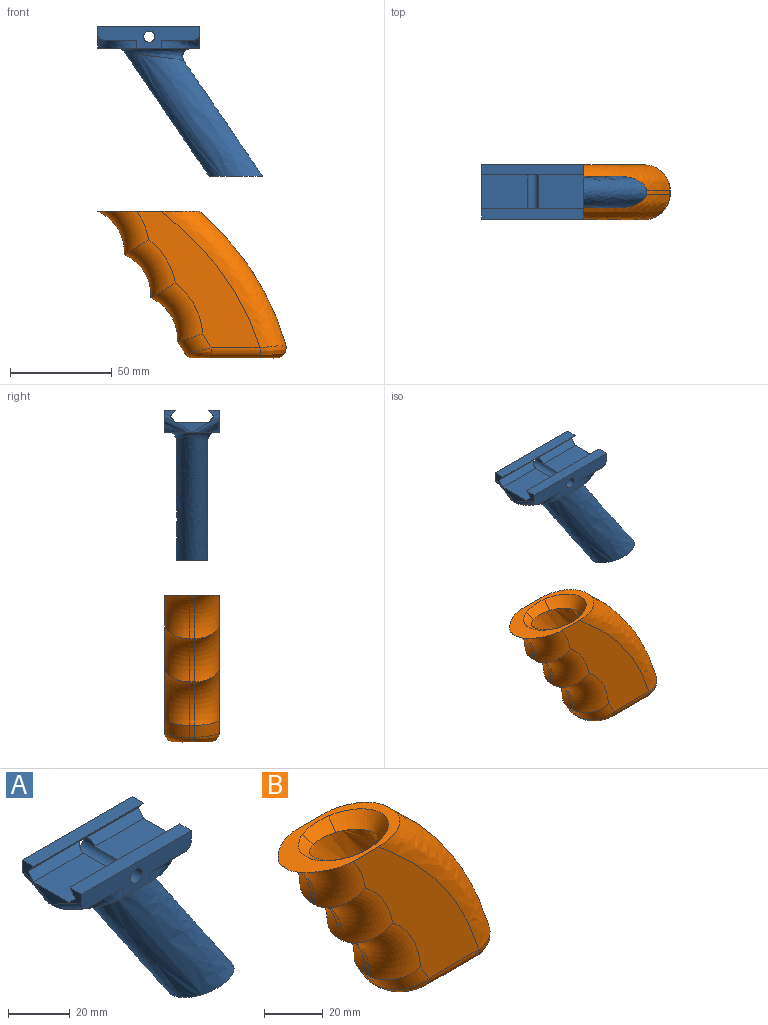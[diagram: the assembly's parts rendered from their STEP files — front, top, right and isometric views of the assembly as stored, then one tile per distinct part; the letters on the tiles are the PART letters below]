
ASSEMBLY  parts=2 mates=1
PART A: 27 faces, bbox 82.1x35.2x74.9 mm
  f0: plane 24x3.29mm, normal (0,0.77,0.64), area 89.2mm2, adj f1,f6,f9,f25
  f1: plane 22.68x16.5mm, normal (0,0,1), area 374.2mm2, adj f0,f6,f12,f25
  f2: plane 23.59x3.23mm, normal (0,-0.77,0.64), area 87.8mm2, adj f4,f11,f13,f25
  f3: plane 50.29x5.25mm, normal (0,0,1), area 264mm2, adj f4,f5,f6,f13
  f4: plane 27x11mm, normal (1,0,0), area 83.6mm2, adj f2,f3,f5,f7,f8,f9,f10,f11
  f5: plane 50.86x11.57mm, normal (0,1,0), area 373mm2, adj f3,f4,f6,f14,f17,f18,f21,f24
  f6: plane 27.33x11.33mm, normal (-1,0,0), area 78mm2, adj f0,f1,f3,f5,f7,f8,f9,f12
  f7: plane 50.86x11.57mm, normal (0,-1,0), area 372.8mm2, adj f4,f6,f8,f14,f15,f16,f22,f23
  f8: plane 50.29x5.25mm, normal (0,0,1), area 264mm2, adj f4,f6,f7,f9
  f9: plane 51.16x3.87mm, normal (0,0.77,-0.64), area 194.9mm2, adj f0,f4,f6,f8,f10,f25
  f10: plane 23.59x3.23mm, normal (0,0.77,0.64), area 87.8mm2, adj f4,f9,f11,f25
  f11: plane 22.33x16.5mm, normal (0,0,1), area 368.5mm2, adj f2,f4,f10,f25
  f12: plane 24x3.29mm, normal (0,-0.77,0.64), area 89.2mm2, adj f1,f6,f13,f25
  f13: plane 51.16x3.87mm, normal (0,-0.77,-0.64), area 194.9mm2, adj f2,f3,f4,f6,f12,f25
  f14: plane 50.72x27.43mm, normal (0,0,-1), area 466.7mm2, adj f4,f5,f6,f7,f15,f16,f17,f18
  f15: bspline ~22.9x10mm, area 89.5mm2, adj f7,f14,f23
  f16: bspline ~31.59x12.5mm, area 86.5mm2, adj f7,f14,f22
  f17: bspline ~31.59x12.5mm, area 89.7mm2, adj f5,f14,f21
  f18: bspline ~18.1x9.17mm, area 89.5mm2, adj f5,f14,f24
  f19: plane 26.94x15.99mm, normal (0,0,-1), area 318.5mm2, adj f20
  f20: bspline ~68.12x61.25mm, area 4200mm2, adj f19,f26
  f21: bspline ~14.67x7.7mm, area 40.7mm2, adj f4,f5,f14,f17
  f22: bspline ~16.64x8.51mm, area 40.8mm2, adj f4,f7,f14,f16
  f23: bspline ~17.09x9.64mm, area 45.5mm2, adj f6,f7,f14,f15
  f24: bspline ~16.58x9.36mm, area 45.5mm2, adj f5,f6,f14,f18
  f25: cylinder r=2.75mm len=27mm, axis (0,-1,0), area 263.8mm2, adj f0,f1,f2,f5,f7,f9,f10,f11
  f26: bspline ~36.01x23.37mm, area 493.5mm2, adj f14,f20
PART B: 33 faces, bbox 113.9x32.2x129.4 mm
  f0: plane 55.28x31.99mm, normal (0,0,1), area 457.1mm2, adj f1,f6,f7,f8,f9,f10,f14,f15
  f1: cylinder r=21.78mm len=21.32mm, axis (0,1,0), area 53.3mm2, adj f0,f2,f10,f15
  f2: cylinder r=21.78mm len=21.32mm, axis (0,1,0), area 53.3mm2, adj f1,f3,f11,f16
  f3: cylinder r=21.78mm len=21.32mm, axis (0,1,0), area 53.3mm2, adj f2,f4,f12,f17
  f4: plane 5.83x3.57mm, normal (-0.85,0,-0.52), area 13.7mm2, adj f3,f13,f18,f20
  f5: plane 40.69x17mm, normal (0,0,-1), area 638.3mm2, adj f19,f20,f21,f22,f23,f24,f25,f26
  f6: extruded ~65.77x42.23mm, area 158.5mm2, adj f0,f9,f14,f25
  f7: plane 67.22x60.73mm, normal (0,-1,0), area 1507.3mm2, adj f0,f14,f15,f16,f17,f18,f21
  f8: plane 67.22x60.73mm, normal (0,1,0), area 1507.2mm2, adj f0,f9,f10,f11,f12,f13,f24
  f9: bspline ~124.44x108.5mm, area 1621.5mm2, adj f0,f6,f8,f26
  f10: torus R=34.28mm, axis (0,-1,0), area 414.5mm2, adj f0,f1,f8,f11
  f11: torus R=34.28mm, axis (0,-1,0), area 498.7mm2, adj f2,f8,f10,f12
  f12: torus R=34.28mm, axis (0,-1,0), area 529.8mm2, adj f3,f8,f11,f13
  f13: cylinder r=12.5mm len=16.63mm, axis (0.52,0,-0.85), area 145.4mm2, adj f4,f8,f12,f22
  f14: bspline ~86.95x66.4mm, area 1621.4mm2, adj f0,f6,f7,f23
  f15: torus R=34.28mm, axis (0,-1,0), area 414.5mm2, adj f0,f1,f7,f16
  f16: torus R=34.28mm, axis (0,-1,0), area 498.7mm2, adj f2,f7,f15,f17
  f17: torus R=34.28mm, axis (0,-1,0), area 529.8mm2, adj f3,f7,f16,f18
  f18: cylinder r=12.5mm len=16.63mm, axis (-0.52,0,0.85), area 145.4mm2, adj f4,f7,f17,f19
  f19: bspline ~13.06x12.5mm, area 104.8mm2, adj f5,f18,f20,f21
  f20: cylinder r=5mm len=4.26mm, axis (0,-1,0), area 10.2mm2, adj f4,f5,f19,f22
  f21: cylinder r=5mm len=24.07mm, axis (-1,0,0), area 189mm2, adj f5,f7,f19,f23
  f22: bspline ~13.06x12.5mm, area 104.8mm2, adj f5,f13,f20,f24
  f23: bspline ~15.72x15.24mm, area 151.9mm2, adj f5,f14,f21,f25
  f24: cylinder r=5mm len=24.07mm, axis (1,0,0), area 189mm2, adj f5,f8,f22,f26
  f25: cylinder r=5mm len=6.4mm, axis (0,1,0), area 18.5mm2, adj f5,f6,f23,f26
  f26: bspline ~17.42x15.74mm, area 151.9mm2, adj f5,f9,f24,f25
  f27: plane 26.94x15.99mm, normal (0,0,1), area 318.5mm2, adj f28
  f28: bspline ~68.07x61.19mm, area 4190.6mm2, adj f27,f29,f30,f31,f32
  f29: bspline ~23.01x14.52mm, area 230.6mm2, adj f0,f28,f30,f31
  f30: bspline ~14.17x5.65mm, area 75.1mm2, adj f0,f28,f29,f32
  f31: bspline ~14.17x5.66mm, area 75.2mm2, adj f0,f28,f29,f32
  f32: bspline ~19.97x9.87mm, area 102.7mm2, adj f0,f28,f30,f31
PLACE A at identity fixed
PLACE B t=(0,0,-74.69)mm
MATE slider B.f27 <-> A.f19  axis (0,0,1) through (28.21,-13.49,-143.19)mm
